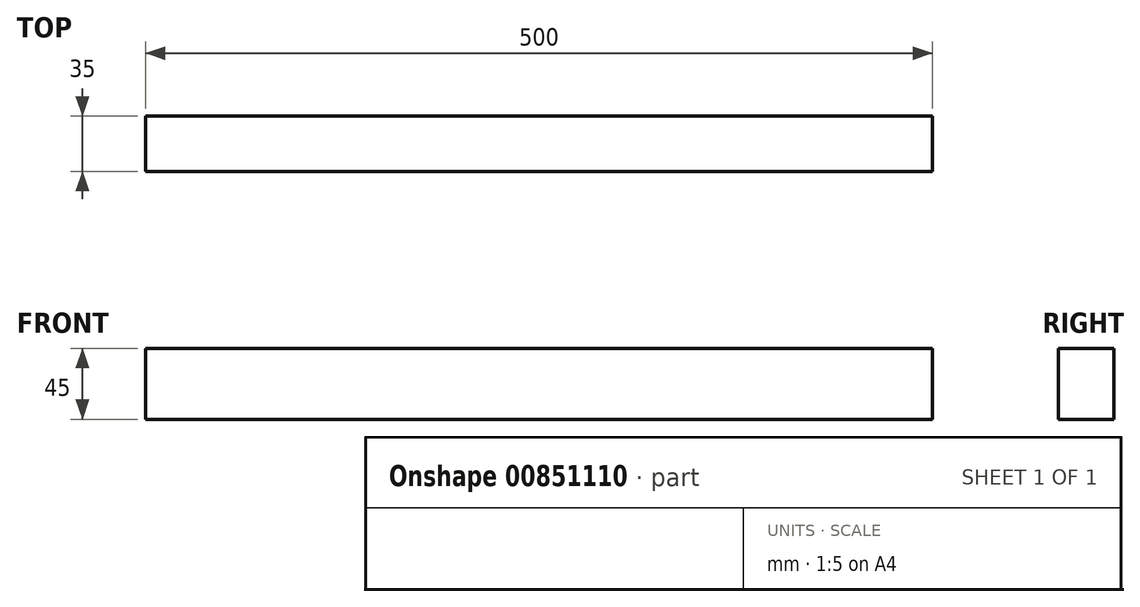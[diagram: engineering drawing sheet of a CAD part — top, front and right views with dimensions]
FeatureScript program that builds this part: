
annotation { "Feature Type Name" : "Feature", "Feature Type Description" : "" }
export const myFeature = defineFeature(function(context is Context, id is Id, definition is map)
    precondition{}
    {
        {
            var Q0;
            Q0=qCreatedBy(makeId("Right.planeOp"),FACE);
            var sketch = newSketch(context, id + "F0", { "sketchPlane" : qUnion([Q0])});
            skLineSegment(sketch, "E0.bottom", {"start": v(0, 0) * mm, "end": v(-35, 0) * mm});
            skLineSegment(sketch, "E0.top", {"start": v(0, -45) * mm, "end": v(-35, -45) * mm});
            skLineSegment(sketch, "E0.left", {"start": v(0, 0) * mm, "end": v(0, -45) * mm});
            skLineSegment(sketch, "E0.right", {"start": v(-35, 0) * mm, "end": v(-35, -45) * mm});
            skSolve(sketch);
        }
        {
            var Q0;
            Q0 = qSketchRegion(id + "F0", true);
            extrude(context, id + "F1", {"entities" : qUnion([Q0]), "oppositeDirection" : true, "depth" : 500 * mm, "offsetDistance" : 25 * mm});
        }
    });
